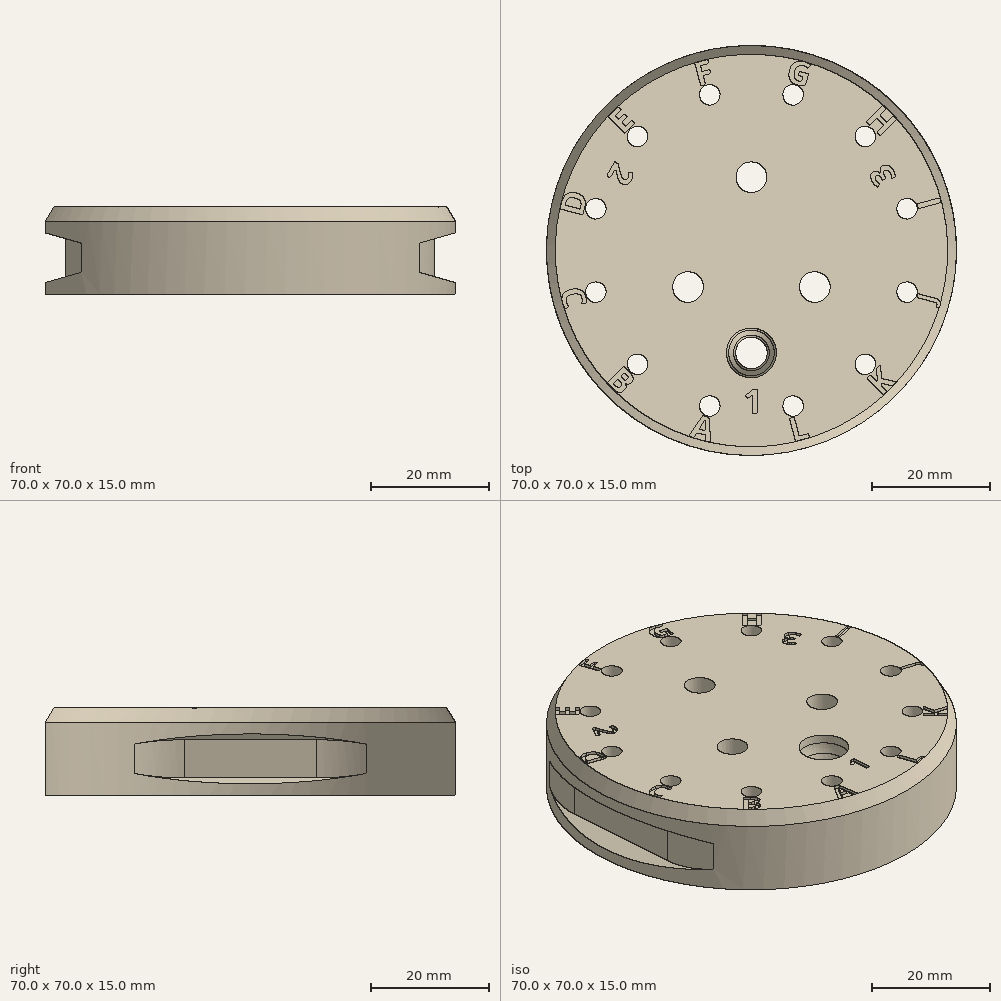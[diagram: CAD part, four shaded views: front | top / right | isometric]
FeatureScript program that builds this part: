
annotation { "Feature Type Name" : "Feature", "Feature Type Description" : "" }
export const myFeature = defineFeature(function(context is Context, id is Id, definition is map)
    precondition{}
    {
        {
            var Q0;
            Q0=qCreatedBy(makeId("Top.planeOp"),FACE);
            var sketch = newSketch(context, id + "F0", { "sketchPlane" : qUnion([Q0])});
            skCircle(sketch, "E0", {"center": v(0, 0) * mm, "radius": 35 * mm});
            skSolve(sketch);
        }
        {
            var Q0;
            Q0=qSketchRegion(id+"F0",true);
            extrude(context, id + "F1", {"entities" : qUnion([Q0]), "depth" : 15 * mm});
        }
        {
            var Q0;
            Q0=qCreatedBy(makeId("Front.planeOp"),FACE);
            var sketch = newSketch(context, id + "F2", { "sketchPlane" : qUnion([Q0])});
            skLineSegment(sketch, "E1", {"start": v(-35, 10.5) * mm, "end": v(-35, 2) * mm});
            skLineSegment(sketch, "E2", {"start": v(-35, 2) * mm, "end": v(-31.5, 3) * mm});
            skLineSegment(sketch, "E3", {"start": v(-31.5, 3) * mm, "end": v(-31.5, 9.5) * mm});
            skLineSegment(sketch, "E4", {"start": v(-31.5, 9.5) * mm, "end": v(-35, 10.5) * mm});
            skLineSegment(sketch, "E5.MirrorCS", {"start": v(35, 10.5) * mm, "end": v(35, 2) * mm});
            skLineSegment(sketch, "E6.MirrorCS", {"start": v(31.5, 9.5) * mm, "end": v(35, 10.5) * mm});
            skLineSegment(sketch, "E7.MirrorCS", {"start": v(35, 2) * mm, "end": v(31.5, 3) * mm});
            skLineSegment(sketch, "E8.MirrorCS", {"start": v(31.5, 3) * mm, "end": v(31.5, 9.5) * mm});
            skSolve(sketch);
        }
        {
            var Q0;
            Q0=qSketchRegion(id+"F2",true);
            extrude(context, id + "F3", {"entities" : qUnion([Q0]), "operationType" : NewBodyOperationType.REMOVE, "endBound" : BoundingType.THROUGH_ALL, "oppositeDirection" : true, "depth" : 25 * mm, "hasSecondDirection" : true, "secondDirectionBound" : SecondDirectionBoundingType.THROUGH_ALL, "secondDirectionOppositeDirection" : false, "secondDirectionDepth" : 25 * mm});
        }
        {
            var Q0;
            {var subQ0=sQuery(id+"F0.wireOp",EDGE,"E0");Q0=makeQuery(id+"F3.boolean.opBoolean","INTERSECT",EDGE,{"disambiguationData":[OD(0.0)],"derivedFrom":[makeQuery(id+"FLbTWpatOgGcuB9_1.boolean.opBoolean","SPLIT",FACE,{"disambiguationData":[TD([makeQuery(id+"F1.opExtrude","CAP_FACE",FACE,{"disambiguationData":[OSD([subQ0])],"isStart":true})])],"derivedFrom":makeQuery(id+"F1.opExtrude","SWEPT_FACE",FACE,{"disambiguationData":[OSD([subQ0])]})}),makeQuery(id+"F3.opExtrude","SWEPT_FACE",FACE,{"disambiguationData":[OSD([sQuery(id+"F2.wireOp",EDGE,"E3")])]})]});}
            var Q1;
            {var subQ0=sQuery(id+"F0.wireOp",EDGE,"E0");Q1=makeQuery(id+"F3.boolean.opBoolean","INTERSECT",EDGE,{"disambiguationData":[OD(0.0)],"derivedFrom":[makeQuery(id+"FLbTWpatOgGcuB9_1.boolean.opBoolean","SPLIT",FACE,{"disambiguationData":[TD([makeQuery(id+"F1.opExtrude","CAP_FACE",FACE,{"disambiguationData":[OSD([subQ0])],"isStart":true})])],"derivedFrom":makeQuery(id+"F1.opExtrude","SWEPT_FACE",FACE,{"disambiguationData":[OSD([subQ0])]})}),makeQuery(id+"F3.opExtrude","SWEPT_FACE",FACE,{"disambiguationData":[OSD([sQuery(id+"F2.wireOp",EDGE,"E8.MirrorCS")])]})]});}
            var Q2;
            {var subQ0=sQuery(id+"F0.wireOp",EDGE,"E0");Q2=makeQuery(id+"F3.boolean.opBoolean","INTERSECT",EDGE,{"disambiguationData":[OD(1.0)],"derivedFrom":[makeQuery(id+"FLbTWpatOgGcuB9_1.boolean.opBoolean","SPLIT",FACE,{"disambiguationData":[TD([makeQuery(id+"F1.opExtrude","CAP_FACE",FACE,{"disambiguationData":[OSD([subQ0])],"isStart":true})])],"derivedFrom":makeQuery(id+"F1.opExtrude","SWEPT_FACE",FACE,{"disambiguationData":[OSD([subQ0])]})}),makeQuery(id+"F3.opExtrude","SWEPT_FACE",FACE,{"disambiguationData":[OSD([sQuery(id+"F2.wireOp",EDGE,"E8.MirrorCS")])]})]});}
            var Q3;
            {var subQ0=sQuery(id+"F0.wireOp",EDGE,"E0");Q3=makeQuery(id+"F3.boolean.opBoolean","INTERSECT",EDGE,{"disambiguationData":[OD(1.0)],"derivedFrom":[makeQuery(id+"FLbTWpatOgGcuB9_1.boolean.opBoolean","SPLIT",FACE,{"disambiguationData":[TD([makeQuery(id+"F1.opExtrude","CAP_FACE",FACE,{"disambiguationData":[OSD([subQ0])],"isStart":true})])],"derivedFrom":makeQuery(id+"F1.opExtrude","SWEPT_FACE",FACE,{"disambiguationData":[OSD([subQ0])]})}),makeQuery(id+"F3.opExtrude","SWEPT_FACE",FACE,{"disambiguationData":[OSD([sQuery(id+"F2.wireOp",EDGE,"E3")])]})]});}
            fillet(context, id + "F4", {"entities" : qUnion([Q0, Q1, Q2, Q3]), "radius" : 15 * mm, "tangentPropagation" : true, "allowEdgeOverflow" : false});
        }
        {
            var Q0;
            Q0=makeQuery(id+"F1.opExtrude","CAP_FACE",FACE,{"disambiguationData":[OSD([sQuery(id+"F0.wireOp",EDGE,"E0")])],"isStart":false});
            var sketch = newSketch(context, id + "F5", { "sketchPlane" : qUnion([Q0])});
            skCircle(sketch, "E9", {"center": v(0, 12.5) * mm, "radius": 2.62 * mm});
            skCircle(sketch, "E10.1.0", {"center": v(-10.83, -6.25) * mm, "radius": 2.62 * mm});
            skCircle(sketch, "E10.2.0", {"center": v(10.83, -6.25) * mm, "radius": 2.62 * mm});
            skPoint(sketch, "E10.center", {"position": v(0, 0) * mm});
            skCircle(sketch, "E11", {"center": v(0, 0) * mm, "radius": 12.5 * mm, "construction": true});
            skSolve(sketch);
        }
        {
            var Q0;
            Q0=qSketchRegion(id+"F5",true);
            extrude(context, id + "F6", {"entities" : qUnion([Q0]), "operationType" : NewBodyOperationType.REMOVE, "endBound" : BoundingType.THROUGH_ALL, "oppositeDirection" : true, "depth" : 25 * mm});
        }
        {
            var Q0;
            Q0=makeQuery(id+"F1.opExtrude","CAP_FACE",FACE,{"disambiguationData":[OSD([sQuery(id+"F0.wireOp",EDGE,"E0")])],"isStart":false});
            var sketch = newSketch(context, id + "F7", { "sketchPlane" : qUnion([Q0])});
            skCircle(sketch, "E12", {"center": v(0, -17.5) * mm, "radius": 2.68 * mm});
            skCircle(sketch, "E13", {"center": v(0, 0) * mm, "radius": 17.5 * mm, "construction": true});
            skSolve(sketch);
        }
        {
            var Q0;
            Q0=qSketchRegion(id+"F7",true);
            extrude(context, id + "F8", {"entities" : qUnion([Q0]), "operationType" : NewBodyOperationType.REMOVE, "endBound" : BoundingType.THROUGH_ALL, "oppositeDirection" : true, "depth" : 25 * mm});
        }
        {
            var Q0;
            Q0=makeQuery(id+"F1.opExtrude","CAP_FACE",FACE,{"disambiguationData":[OSD([sQuery(id+"F0.wireOp",EDGE,"E0")])],"isStart":false});
            var sketch = newSketch(context, id + "F9", { "sketchPlane" : qUnion([Q0])});
            skCircle(sketch, "E14", {"center": v(0, -17.5) * mm, "radius": 4.25 * mm});
            skSolve(sketch);
        }
        {
            var Q0;
            Q0=qSketchRegion(id+"F9",true);
            extrude(context, id + "F10", {"entities" : qUnion([Q0]), "operationType" : NewBodyOperationType.REMOVE, "oppositeDirection" : true, "depth" : 7.5 * mm});
        }
        {
            var Q0;
            Q0=makeQuery(id+"F10.boolean.opBoolean","COPY",EDGE,{"derivedFrom":makeQuery(id+"F10.opExtrude","CAP_EDGE",EDGE,{"disambiguationData":[OSD([sQuery(id+"F9.wireOp",EDGE,"E14")])],"isStart":false})});
            chamfer(context, id + "F11", {"entities" : qUnion([Q0]), "chamferType" : ChamferType.TWO_OFFSETS, "width1" : 5 * mm, "oppositeDirection" : true, "width2" : 2 * mm, "tangentPropagation" : true});
        }
        {
            var Q0;
            {var subQ0=sQuery(id+"F9.wireOp",EDGE,"E14");Q0=makeQuery(id+"F11.opChamfer","BLEND_EDGE",EDGE,{"blendedFrom":[makeQuery(id+"F10.boolean.opBoolean","COPY",EDGE,{"derivedFrom":makeQuery(id+"F10.opExtrude","CAP_EDGE",EDGE,{"disambiguationData":[OSD([subQ0])],"isStart":false})}),makeQuery(id+"F10.boolean.opBoolean","COPY",FACE,{"derivedFrom":makeQuery(id+"F10.opExtrude","SWEPT_FACE",FACE,{"disambiguationData":[OSD([subQ0])]})})],"blendedInto":[makeQuery(id+"F10.boolean.opBoolean","COPY",FACE,{"derivedFrom":makeQuery(id+"F10.opExtrude","SWEPT_FACE",FACE,{"disambiguationData":[OSD([subQ0])]})})]});}
            var Q1;
            Q1=makeQuery(id+"F11.opChamfer","BLEND_EDGE",EDGE,{"blendedFrom":[makeQuery(id+"F10.boolean.opBoolean","COPY",EDGE,{"derivedFrom":makeQuery(id+"F10.opExtrude","CAP_EDGE",EDGE,{"disambiguationData":[OSD([sQuery(id+"F9.wireOp",EDGE,"E14")])],"isStart":false})}),makeQuery(id+"F8.boolean.opBoolean","COPY",FACE,{"derivedFrom":makeQuery(id+"F8.opExtrude","SWEPT_FACE",FACE,{"disambiguationData":[OSD([sQuery(id+"F7.wireOp",EDGE,"E12")])]})})],"blendedInto":[makeQuery(id+"F8.boolean.opBoolean","COPY",FACE,{"derivedFrom":makeQuery(id+"F8.opExtrude","SWEPT_FACE",FACE,{"disambiguationData":[OSD([sQuery(id+"F7.wireOp",EDGE,"E12")])]})})]});
            fillet(context, id + "F12", {"entities" : qUnion([Q0, Q1]), "radius" : 5 * mm, "tangentPropagation" : true, "allowEdgeOverflow" : false});
        }
        {
            var Q0;
            Q0=makeQuery(id+"F1.opExtrude","CAP_FACE",FACE,{"disambiguationData":[OSD([sQuery(id+"F0.wireOp",EDGE,"E0")])],"isStart":false});
            var sketch = newSketch(context, id + "F13", { "sketchPlane" : qUnion([Q0])});
            skCircle(sketch, "E15", {"center": v(19.45, 19.45) * mm, "radius": 1.75 * mm});
            skCircle(sketch, "E16", {"center": v(0, 0) * mm, "radius": 27.5 * mm, "construction": true});
            skLineSegment(sketch, "E17", {"start": v(0, 0) * mm, "end": v(19.45, 19.45) * mm, "construction": true});
            skCircle(sketch, "E18.1.1", {"center": v(7.12, 26.56) * mm, "radius": 1.75 * mm});
            skCircle(sketch, "E18.2.1", {"center": v(-7.12, 26.56) * mm, "radius": 1.75 * mm});
            skCircle(sketch, "E18.3.1", {"center": v(-19.45, 19.45) * mm, "radius": 1.75 * mm});
            skCircle(sketch, "E18.4.1", {"center": v(-26.56, 7.12) * mm, "radius": 1.75 * mm});
            skCircle(sketch, "E18.5.1", {"center": v(-26.56, -7.12) * mm, "radius": 1.75 * mm});
            skCircle(sketch, "E18.6.1", {"center": v(-19.45, -19.45) * mm, "radius": 1.75 * mm});
            skCircle(sketch, "E18.7.1", {"center": v(-7.12, -26.56) * mm, "radius": 1.75 * mm});
            skCircle(sketch, "E18.8.1", {"center": v(7.12, -26.56) * mm, "radius": 1.75 * mm});
            skCircle(sketch, "E18.9.1", {"center": v(19.45, -19.45) * mm, "radius": 1.75 * mm});
            skCircle(sketch, "E18.10.1", {"center": v(26.56, -7.12) * mm, "radius": 1.75 * mm});
            skCircle(sketch, "E18.11.1", {"center": v(26.56, 7.12) * mm, "radius": 1.75 * mm});
            skSolve(sketch);
        }
        {
            var Q0;
            Q0=qSketchRegion(id+"F13",true);
            extrude(context, id + "F14", {"entities" : qUnion([Q0]), "operationType" : NewBodyOperationType.REMOVE, "endBound" : BoundingType.THROUGH_ALL, "oppositeDirection" : true, "depth" : 25 * mm});
        }
        {
            var Q0;
            Q0=makeQuery(id+"F1.opExtrude","CAP_EDGE",EDGE,{"disambiguationData":[OSD([sQuery(id+"F0.wireOp",EDGE,"E0")])],"isStart":false});
            chamfer(context, id + "F15", {"entities" : qUnion([Q0]), "chamferType" : ChamferType.TWO_OFFSETS, "width1" : 2.5 * mm, "oppositeDirection" : true, "width2" : 1.5 * mm, "tangentPropagation" : true});
        }
        {
            var Q0;
            Q0=makeQuery(id+"F1.opExtrude","CAP_FACE",FACE,{"disambiguationData":[OSD([sQuery(id+"F0.wireOp",EDGE,"E0")])],"isStart":false});
            var sketch = newSketch(context, id + "F16", { "sketchPlane" : qUnion([Q0])});
            skText(sketch, "E19", { "text": "A", "fontName": "OpenSans-Bold.ttf"});
            skText(sketch, "E20", { "text": "B", "fontName": "OpenSans-Bold.ttf"});
            skText(sketch, "E21", { "text": "C", "fontName": "OpenSans-Bold.ttf"});
            skText(sketch, "E22", { "text": "E", "fontName": "OpenSans-Bold.ttf"});
            skText(sketch, "E23", { "text": "F", "fontName": "OpenSans-Bold.ttf"});
            skText(sketch, "E24", { "text": "G", "fontName": "OpenSans-Bold.ttf"});
            skText(sketch, "E25", { "text": "H", "fontName": "OpenSans-Bold.ttf"});
            skText(sketch, "E26", { "text": "I", "fontName": "OpenSans-Bold.ttf"});
            skText(sketch, "E27", { "text": "J", "fontName": "OpenSans-Bold.ttf"});
            skText(sketch, "E28", { "text": "K", "fontName": "OpenSans-Bold.ttf"});
            skText(sketch, "E29", { "text": "L", "fontName": "OpenSans-Bold.ttf"});
            skText(sketch, "E30", { "text": "D", "fontName": "OpenSans-Bold.ttf"});
            skCircle(sketch, "E31", {"center": v(0, 0) * mm, "radius": 29.38 * mm, "construction": true});
            skText(sketch, "E32", { "text": "1", "fontName": "OpenSans-Bold.ttf"});
            skText(sketch, "E33", { "text": "2", "fontName": "OpenSans-Bold.ttf"});
            skText(sketch, "E34", { "text": "3", "fontName": "OpenSans-Bold.ttf"});
            skCircle(sketch, "E35", {"center": v(0, 0) * mm, "radius": 23.75 * mm, "construction": true});
            const initialGuessF16  = {"E19": [-0.0107, -0.03174, 0.96593, -0.25882, 0.00406], "E20": [-0.025, -0.02228, 0.7071, -0.7071, 0.00406], "E21": [-0.03278, -0.00684, 0.25882, -0.96593, 0.00406], "E22": [-0.0219, 0.01964, 0.7071, 0.7071, 0.00406], "E23": [-0.00914, 0.02796, 0.96593, 0.25882, 0.00406], "E24": [0.00567, 0.0289, 0.96593, -0.25882, 0.00406], "E25": [0.0193, 0.02225, 0.7071, -0.7071, 0.00406], "E26": [0.02815, 0.00844, 0.25882, -0.96593, 0.00406], "E27": [0.0313, -0.00927, 0.25882, 0.96593, 0.00325], "E28": [0.02219, -0.0251, 0.7071, 0.7071, 0.00406], "E29": [0.00703, -0.03273, 0.96593, 0.25882, 0.00406], "E30": [-0.02892, 0.00557, 0.25882, 0.96593, 0.00406], "E32": [-0.00133, -0.02775, 1, 0, 0.004], "E33": [-0.0232, 0.01533, -0.5, -0.86603, 0.004], "E34": [0.02486, 0.01244, -0.5, 0.86603, 0.004]};
            skSetInitialGuess(sketch, initialGuessF16);
            skSolve(sketch);
        }
        {
            var Q0;
            Q0=qSketchRegion(id+"F16",true);
            extrude(context, id + "F17", {"entities" : qUnion([Q0]), "operationType" : NewBodyOperationType.REMOVE, "oppositeDirection" : true, "depth" : .5 * mm});
        }
    });
